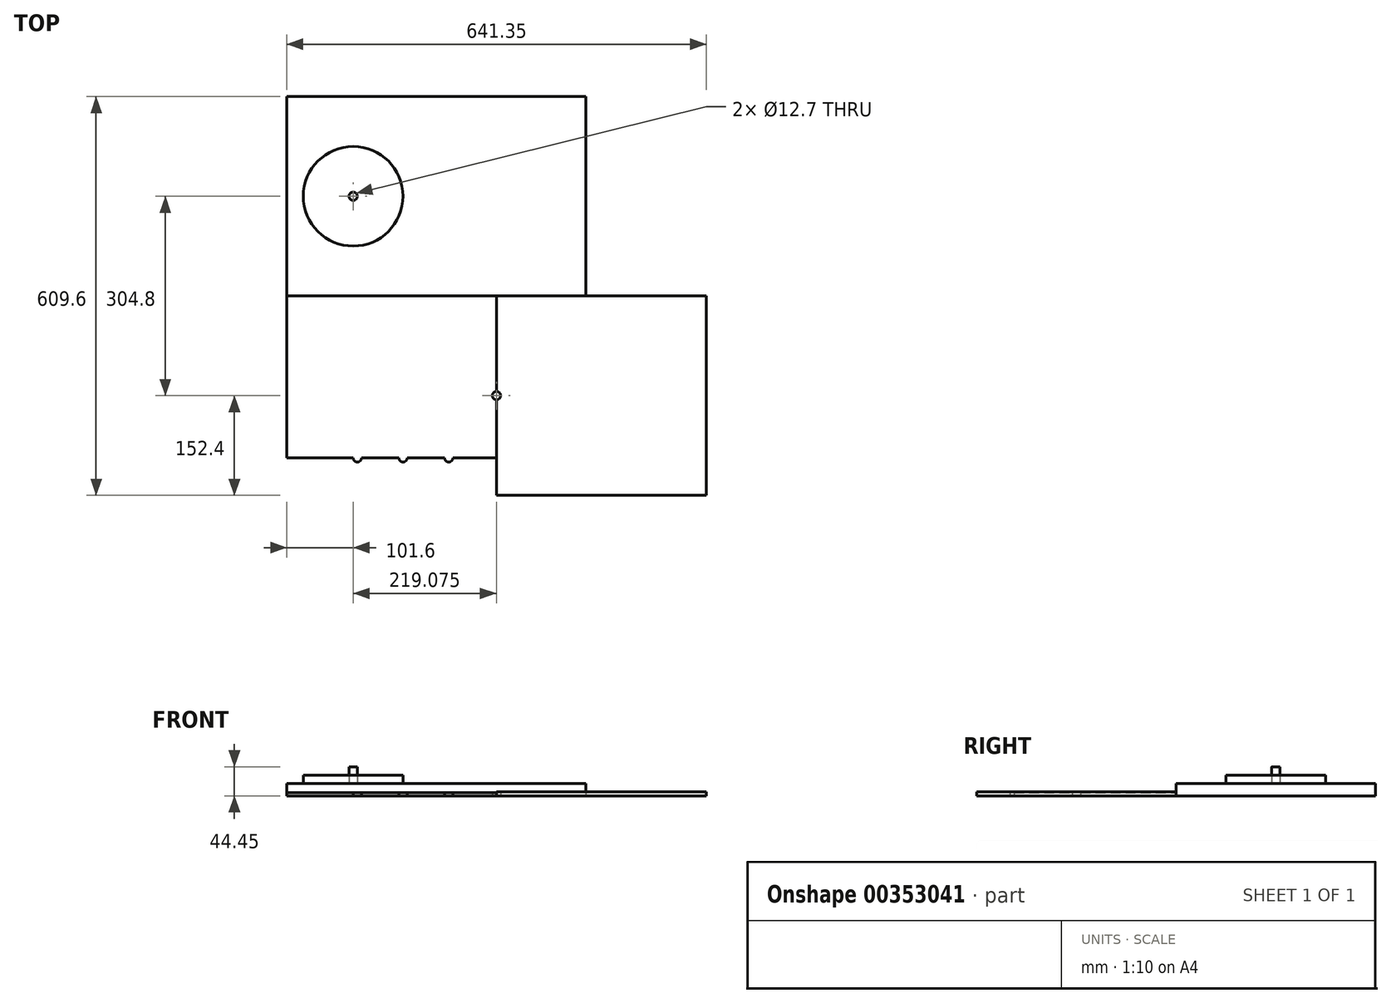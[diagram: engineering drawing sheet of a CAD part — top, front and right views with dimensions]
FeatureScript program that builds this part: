
annotation { "Feature Type Name" : "Feature", "Feature Type Description" : "" }
export const myFeature = defineFeature(function(context is Context, id is Id, definition is map)
    precondition{}
    {
        {
            var Q0;
            Q0=qCreatedBy(makeId("Top.planeOp"),FACE);
            var sketch = newSketch(context, id + "F0", { "sketchPlane" : qUnion([Q0])});
            skLineSegment(sketch, "E0.bottom", {"start": v(0, 0) * mm, "end": v(457.2, 0) * mm});
            skLineSegment(sketch, "E0.top", {"start": v(0, 304.8) * mm, "end": v(457.2, 304.8) * mm});
            skLineSegment(sketch, "E0.left", {"start": v(0, 0) * mm, "end": v(0, 304.8) * mm});
            skLineSegment(sketch, "E0.right", {"start": v(457.2, 0) * mm, "end": v(457.2, 304.8) * mm});
            skSolve(sketch);
        }
        {
            var Q0;
            Q0=makeQuery(id+"F0.imprint","IMPRINT",FACE,{"disambiguationData":[TD([[makeQuery(id+"F0.imprint","IMPRINT",EDGE,{"derivedFrom":sQuery(id+"F0.wireOp",EDGE,"E0.bottom")}),1.0]])]});
            extrude(context, id + "F1", {"entities" : qUnion([Q0]), "depth" : 19.05 * mm});
        }
        {
            var Q0;
            Q0=makeQuery(id+"F1.opExtrude","CAP_FACE",FACE,{"disambiguationData":[OSD([sQuery(id+"F0.wireOp",EDGE,"E0.bottom"),sQuery(id+"F0.wireOp",EDGE,"E0.top"),sQuery(id+"F0.wireOp",EDGE,"E0.left"),sQuery(id+"F0.wireOp",EDGE,"E0.right")])],"isStart":false});
            var sketch = newSketch(context, id + "F2", { "sketchPlane" : qUnion([Q0])});
            skLineSegment(sketch, "E1.0", {"start": v(101.6, 0) * mm, "end": v(101.6, 304.8) * mm, "construction": true});
            skLineSegment(sketch, "E2.0", {"start": v(0, 152.4) * mm, "end": v(457.2, 152.4) * mm, "construction": true});
            skCircle(sketch, "E3", {"center": v(101.6, 152.4) * mm, "radius": 76.2 * mm});
            skCircle(sketch, "E4", {"center": v(101.6, 152.4) * mm, "radius": 6.35 * mm});
            skSolve(sketch);
        }
        {
            var Q0;
            Q0=makeQuery(id+"F2.imprint","IMPRINT",FACE,{"disambiguationData":[TD([[makeQuery(id+"F2.imprint","IMPRINT",EDGE,{"derivedFrom":sQuery(id+"F2.wireOp",EDGE,"E3")}),1.0]])]});
            extrude(context, id + "F3", {"entities" : qUnion([Q0]), "depth" : 12.7 * mm});
        }
        {
            var Q0;
            Q0=makeQuery(id+"F2.imprint","IMPRINT",FACE,{"disambiguationData":[TD([[makeQuery(id+"F2.imprint","IMPRINT",EDGE,{"derivedFrom":sQuery(id+"F2.wireOp",EDGE,"E4")}),1.0]])]});
            extrude(context, id + "F4", {"entities" : qUnion([Q0]), "depth" : 25.4 * mm});
        }
        {
            var Q0;
            Q0=qCreatedBy(makeId("Top.planeOp"),FACE);
            var sketch = newSketch(context, id + "F5", { "sketchPlane" : qUnion([Q0])});
            skLineSegment(sketch, "E5.bottom", {"start": v(0, 0) * mm, "end": v(641.35, 0) * mm});
            skLineSegment(sketch, "E5.top", {"start": v(0, -304.8) * mm, "end": v(641.35, -304.8) * mm});
            skLineSegment(sketch, "E5.left", {"start": v(0, 0) * mm, "end": v(0, -304.8) * mm});
            skLineSegment(sketch, "E5.right", {"start": v(641.35, 0) * mm, "end": v(641.35, -304.8) * mm});
            skLineSegment(sketch, "E6", {"start": v(0, -304.8) * mm, "end": v(0, -81.52) * mm});
            skLineSegment(sketch, "E7", {"start": v(0, 0) * mm, "end": v(0, -247.65) * mm});
            skLineSegment(sketch, "E8", {"start": v(0, -247.65) * mm, "end": v(641.35, -247.65) * mm, "construction": true});
            skLineSegment(sketch, "E9", {"start": v(0, -247.65) * mm, "end": v(107.95, -247.65) * mm});
            skCircle(sketch, "E10", {"center": v(107.95, -247.65) * mm, "radius": 6.35 * mm});
            skLineSegment(sketch, "E11", {"start": v(107.95, -247.65) * mm, "end": v(177.8, -247.65) * mm});
            skCircle(sketch, "E12", {"center": v(177.8, -247.65) * mm, "radius": 6.35 * mm});
            skLineSegment(sketch, "E13", {"start": v(177.8, -247.65) * mm, "end": v(247.65, -247.65) * mm});
            skCircle(sketch, "E14", {"center": v(247.65, -247.65) * mm, "radius": 6.35 * mm});
            skLineSegment(sketch, "E15", {"start": v(247.65, -247.65) * mm, "end": v(320.68, -247.65) * mm});
            skLineSegment(sketch, "E16", {"start": v(320.68, -247.65) * mm, "end": v(320.68, 0) * mm});
            skLineSegment(sketch, "E17", {"start": v(320.68, -247.65) * mm, "end": v(320.68, -304.8) * mm});
            skLineSegment(sketch, "E18", {"start": v(0, 0) * mm, "end": v(0, -152.4) * mm});
            skLineSegment(sketch, "E19", {"start": v(0, -152.4) * mm, "end": v(47.63, -152.4) * mm});
            skLineSegment(sketch, "E20", {"start": v(320.68, 0) * mm, "end": v(320.68, -16.55) * mm});
            skLineSegment(sketch, "E21", {"start": v(320.68, 0) * mm, "end": v(320.68, -152.4) * mm});
            skCircle(sketch, "E22", {"center": v(320.68, -152.4) * mm, "radius": 6.35 * mm});
            skCircle(sketch, "E23", {"center": v(47.63, -152.4) * mm, "radius": 44.45 * mm});
            skSolve(sketch);
        }
        {
            var Q0;
            {var subQ0=sQuery(id+"F5.wireOp",EDGE,"E5.right");Q0=makeQuery(id+"F5.imprint","IMPRINT",FACE,{"disambiguationData":[TD([[makeQuery(id+"F5.imprint","IMPRINT",EDGE,{"derivedFrom":subQ0}),-1.0]])]});}
            var Q1;
            {var subQ20=sQuery(id+"F5.wireOp",EDGE,"E7");Q1=makeQuery(id+"F5.imprint","IMPRINT",FACE,{"disambiguationData":[TD([[makeQuery(id+"F5.imprint","IMPRINT",EDGE,{"derivedFrom":subQ20}),1.0]])]});}
            var Q2;
            {var subQ5=sQuery(id+"F5.wireOp",EDGE,"E6");Q2=makeQuery(id+"F5.imprint","IMPRINT",FACE,{"disambiguationData":[TD([[makeQuery(id+"F5.imprint","IMPRINT",EDGE,{"derivedFrom":subQ5}),-1.0]])]});}
            extrude(context, id + "F6", {"entities" : qUnion([Q0, Q1, Q2]), "depth" : 6.35 * mm});
        }
        {
            var Q0;
            Q0=makeQuery(id+"F5.imprint","IMPRINT",FACE,{"disambiguationData":[TD([[makeQuery(id+"F5.imprint","IMPRINT",EDGE,{"derivedFrom":sQuery(id+"F5.wireOp",EDGE,"E23")}),1.0]])]});
            var Q1;
            {var subQ0=sQuery(id+"F5.wireOp",EDGE,"E11");var subQ1=sQuery(id+"F5.wireOp",EDGE,"E9");var subQ2=makeQuery(id+"F5.imprint","INTERSECT",VERTEX,{"derivedFrom":[subQ1,subQ0]});Q1=makeQuery(id+"F5.imprint","IMPRINT",FACE,{"disambiguationData":[TD([[makeQuery(id+"F5.imprint","IMPRINT",EDGE,{"disambiguationData":[TD([[subQ2,1.0]])],"derivedFrom":subQ1}),-1.0]])]});}
            var Q2;
            {var subQ0=sQuery(id+"F5.wireOp",EDGE,"E11");var subQ1=sQuery(id+"F5.wireOp",EDGE,"E9");var subQ2=makeQuery(id+"F5.imprint","INTERSECT",VERTEX,{"derivedFrom":[subQ1,subQ0]});Q2=makeQuery(id+"F5.imprint","IMPRINT",FACE,{"disambiguationData":[TD([[makeQuery(id+"F5.imprint","IMPRINT",EDGE,{"disambiguationData":[TD([[subQ2,1.0]])],"derivedFrom":subQ1}),1.0]])]});}
            var Q3;
            {var subQ0=sQuery(id+"F5.wireOp",EDGE,"E13");var subQ1=sQuery(id+"F5.wireOp",EDGE,"E11");var subQ2=makeQuery(id+"F5.imprint","INTERSECT",VERTEX,{"derivedFrom":[subQ1,subQ0]});Q3=makeQuery(id+"F5.imprint","IMPRINT",FACE,{"disambiguationData":[TD([[makeQuery(id+"F5.imprint","IMPRINT",EDGE,{"disambiguationData":[TD([[subQ2,1.0]])],"derivedFrom":subQ1}),-1.0]])]});}
            var Q4;
            {var subQ0=sQuery(id+"F5.wireOp",EDGE,"E13");var subQ1=sQuery(id+"F5.wireOp",EDGE,"E11");var subQ2=makeQuery(id+"F5.imprint","INTERSECT",VERTEX,{"derivedFrom":[subQ1,subQ0]});Q4=makeQuery(id+"F5.imprint","IMPRINT",FACE,{"disambiguationData":[TD([[makeQuery(id+"F5.imprint","IMPRINT",EDGE,{"disambiguationData":[TD([[subQ2,1.0]])],"derivedFrom":subQ1}),1.0]])]});}
            var Q5;
            {var subQ0=sQuery(id+"F5.wireOp",EDGE,"E15");var subQ1=sQuery(id+"F5.wireOp",EDGE,"E13");var subQ2=makeQuery(id+"F5.imprint","INTERSECT",VERTEX,{"derivedFrom":[subQ1,subQ0]});Q5=makeQuery(id+"F5.imprint","IMPRINT",FACE,{"disambiguationData":[TD([[makeQuery(id+"F5.imprint","IMPRINT",EDGE,{"disambiguationData":[TD([[subQ2,1.0]])],"derivedFrom":subQ1}),-1.0]])]});}
            var Q6;
            {var subQ0=sQuery(id+"F5.wireOp",EDGE,"E15");var subQ1=sQuery(id+"F5.wireOp",EDGE,"E13");var subQ2=makeQuery(id+"F5.imprint","INTERSECT",VERTEX,{"derivedFrom":[subQ1,subQ0]});Q6=makeQuery(id+"F5.imprint","IMPRINT",FACE,{"disambiguationData":[TD([[makeQuery(id+"F5.imprint","IMPRINT",EDGE,{"disambiguationData":[TD([[subQ2,1.0]])],"derivedFrom":subQ1}),1.0]])]});}
            var Q7;
            {var subQ0=sQuery(id+"F5.wireOp",EDGE,"E21");var subQ1=sQuery(id+"F5.wireOp",EDGE,"E16");var subQ2=makeQuery(id+"F5.imprint","INTERSECT",VERTEX,{"derivedFrom":[subQ1,subQ0]});Q7=makeQuery(id+"F5.imprint","IMPRINT",FACE,{"disambiguationData":[TD([[makeQuery(id+"F5.imprint","IMPRINT",EDGE,{"disambiguationData":[TD([[subQ2,1.0]])],"derivedFrom":subQ1}),-1.0]])]});}
            var Q8;
            {var subQ0=sQuery(id+"F5.wireOp",EDGE,"E21");var subQ1=sQuery(id+"F5.wireOp",EDGE,"E16");var subQ2=makeQuery(id+"F5.imprint","INTERSECT",VERTEX,{"derivedFrom":[subQ1,subQ0]});Q8=makeQuery(id+"F5.imprint","IMPRINT",FACE,{"disambiguationData":[TD([[makeQuery(id+"F5.imprint","IMPRINT",EDGE,{"disambiguationData":[TD([[subQ2,1.0]])],"derivedFrom":subQ1}),1.0]])]});}
            extrude(context, id + "F7", {"entities" : qUnion([Q0, Q1, Q2, Q3, Q4, Q5, Q6, Q7, Q8]), "operationType" : NewBodyOperationType.ADD, "depth" : 4.76 * mm});
        }
    });
